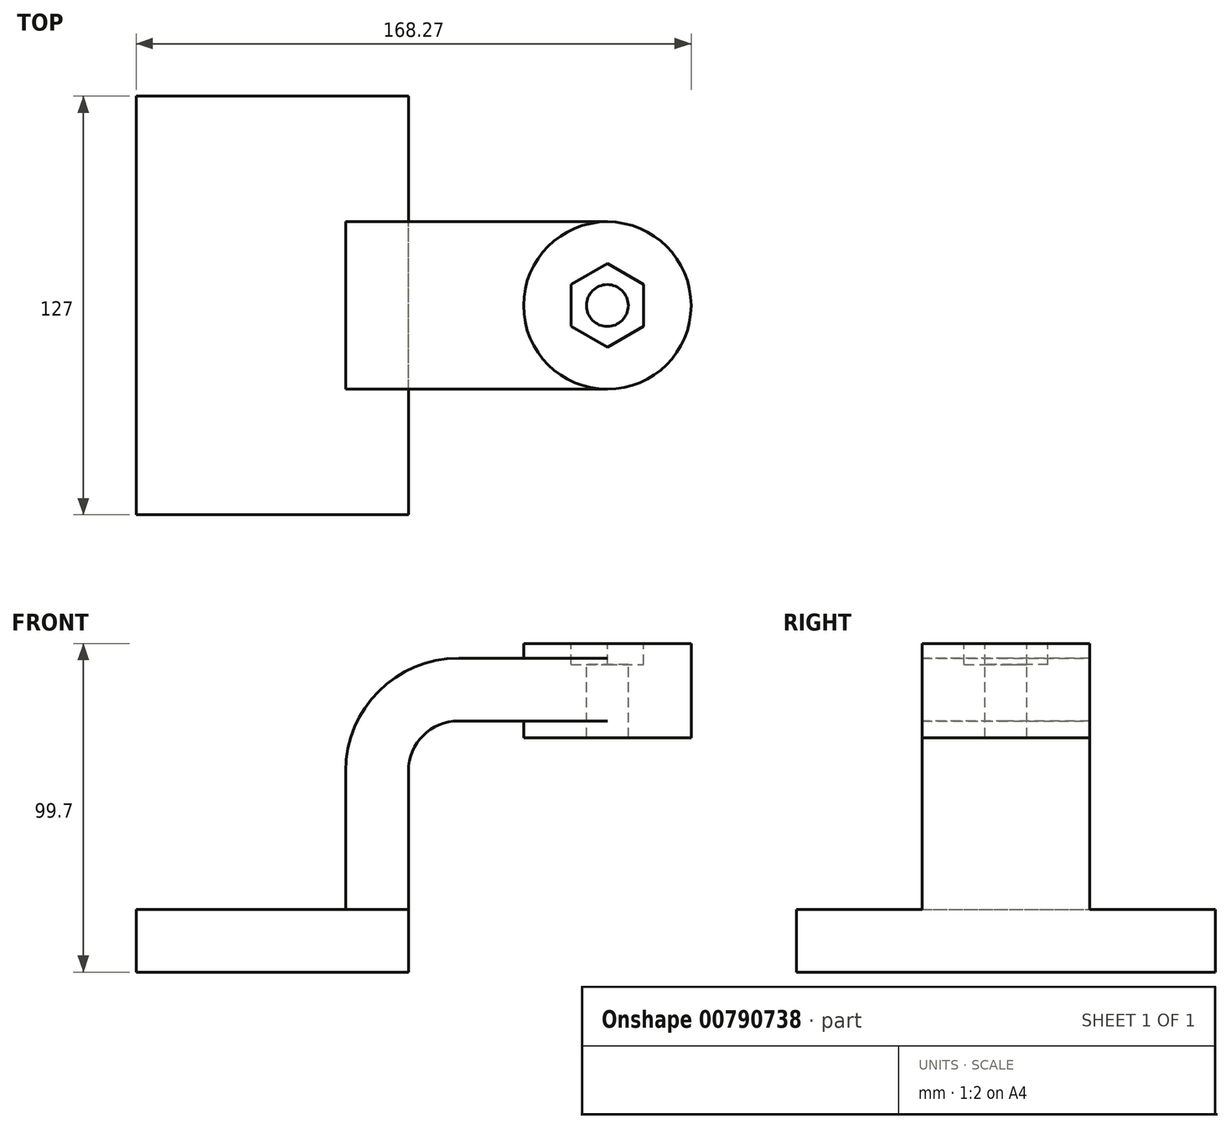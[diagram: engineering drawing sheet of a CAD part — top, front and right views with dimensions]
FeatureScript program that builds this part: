
annotation { "Feature Type Name" : "Feature", "Feature Type Description" : "" }
export const myFeature = defineFeature(function(context is Context, id is Id, definition is map)
    precondition{}
    {
        {
            var Q0;
            Q0=qCreatedBy(makeId("Front.planeOp"),FACE);
            var sketch = newSketch(context, id + "F0", { "sketchPlane" : qUnion([Q0])});
            skLineSegment(sketch, "E0.bottom", {"start": v(-41.28, 9.52) * mm, "end": v(41.28, 9.53) * mm});
            skLineSegment(sketch, "E0.top", {"start": v(-41.28, -9.52) * mm, "end": v(41.28, -9.52) * mm});
            skLineSegment(sketch, "E0.left", {"start": v(-41.28, 9.52) * mm, "end": v(-41.27, -9.53) * mm});
            skLineSegment(sketch, "E0.right", {"start": v(41.28, 9.53) * mm, "end": v(41.28, -9.52) * mm});
            skPoint(sketch, "E0.middle", {"position": v(0, 0) * mm});
            skLineSegment(sketch, "E1.bottom", {"start": v(76.2, 61.6) * mm, "end": v(127, 61.6) * mm});
            skLineSegment(sketch, "E1.top", {"start": v(76.2, 90.17) * mm, "end": v(127, 90.17) * mm});
            skLineSegment(sketch, "E1.left", {"start": v(76.2, 61.6) * mm, "end": v(76.2, 90.17) * mm});
            skLineSegment(sketch, "E1.right", {"start": v(127, 61.6) * mm, "end": v(127, 90.17) * mm});
            skPoint(sketch, "E1.middle", {"position": v(101.6, 75.88) * mm});
            skLineSegment(sketch, "E2", {"start": v(41.27, 9.53) * mm, "end": v(41.27, 51.44) * mm});
            skArc(sketch, "E3", {"start": v(41.27, 51.44) * mm, "mid": v(45.74, 62.21) * mm, "end": v(56.51, 66.68) * mm});
            skLineSegment(sketch, "E4", {"start": v(56.51, 66.68) * mm, "end": v(101.6, 66.68) * mm});
            skArc(sketch, "E5.1", {"start": v(22.22, 51.44) * mm, "mid": v(32.27, 75.68) * mm, "end": v(56.52, 85.73) * mm});
            skLineSegment(sketch, "E5.2", {"start": v(22.23, 9.53) * mm, "end": v(22.23, 51.44) * mm});
            skLineSegment(sketch, "E6.0", {"start": v(56.51, 85.73) * mm, "end": v(101.6, 85.73) * mm});
            skLineSegment(sketch, "E7", {"start": v(101.6, 61.6) * mm, "end": v(101.6, 90.17) * mm});
            skFitSpline(sketch, "E8", {"points": [v(-41.28, 9.53) * mm, v(56.52, 85.73) * mm], "startDerivative": vector(43.08, 48.74) * mm, "endDerivative": vector(237.38, -7.73) * mm});
            skSolve(sketch);
        }
        {
            var Q0;
            Q0=makeQuery(id+"F0.imprint","IMPRINT",FACE,{"disambiguationData":[TD([[makeQuery(id+"F0.imprint","IMPRINT",EDGE,{"derivedFrom":sQuery(id+"F0.wireOp",EDGE,"E0.top")}),1.0]])]});
            extrude(context, id + "F1", {"entities" : qUnion([Q0]), "endBound" : BoundingType.SYMMETRIC, "depth" : 127 * mm, "offsetDistance" : 25.4 * mm});
        }
        {
            var Q0;
            {var subQ1=sQuery(id+"F0.wireOp",EDGE,"E2");Q0=makeQuery(id+"F0.imprint","IMPRINT",FACE,{"disambiguationData":[TD([[makeQuery(id+"F0.imprint","IMPRINT",EDGE,{"derivedFrom":subQ1}),1.0]])]});}
            var Q1;
            {var subQ0=sQuery(id+"F0.wireOp",EDGE,"E4");var subQ1=sQuery(id+"F0.wireOp",EDGE,"E1.left");var subQ2=makeQuery(id+"F0.imprint","INTERSECT",VERTEX,{"derivedFrom":[subQ1,subQ0]});Q1=makeQuery(id+"F0.imprint","IMPRINT",FACE,{"disambiguationData":[TD([[makeQuery(id+"F0.imprint","IMPRINT",EDGE,{"disambiguationData":[TD([[subQ2,-1.0]])],"derivedFrom":subQ1}),-1.0]])]});}
            extrude(context, id + "F2", {"entities" : qUnion([Q0, Q1]), "operationType" : NewBodyOperationType.ADD, "endBound" : BoundingType.SYMMETRIC, "depth" : 50.8 * mm, "offsetDistance" : 25.4 * mm});
        }
        {
            var Q0;
            Q0=makeQuery(id+"F0.imprint","IMPRINT",FACE,{"disambiguationData":[TD([[makeQuery(id+"F0.imprint","IMPRINT",EDGE,{"derivedFrom":sQuery(id+"F0.wireOp",EDGE,"E5.1")}),1.0]])]});
            extrude(context, id + "F3", {"entities" : qUnion([Q0]), "operationType" : NewBodyOperationType.ADD, "endBound" : BoundingType.SYMMETRIC, "depth" : 12.7 * mm, "offsetDistance" : 25.4 * mm});
        }
        {
            var Q0;
            {var subQ0=sQuery(id+"F0.wireOp",EDGE,"E1.right");Q0=makeQuery(id+"F0.imprint","IMPRINT",FACE,{"disambiguationData":[TD([[makeQuery(id+"F0.imprint","IMPRINT",EDGE,{"derivedFrom":subQ0}),1.0]])]});}
            var Q1;
            Q1=sQuery(id+"F0.wireOp",EDGE,"E7");
            revolve(context, id + "F4", {"operationType" : NewBodyOperationType.ADD, "surfaceOperationType" : NewSurfaceOperationType.NEW, "entities" : qUnion([Q0]), "axis" : qUnion([Q1]), "revolveType" : RevolveType.FULL});
        }
        {
            var Q0;
            Q0=makeQuery(id+"F4.opRevolve","SWEPT_FACE",FACE,{"disambiguationData":[OSD([sQuery(id+"F0.wireOp",EDGE,"E1.top")])]});
            var sketch = newSketch(context, id + "F5", { "sketchPlane" : qUnion([Q0])});
            skCircle(sketch, "E9", {"center": v(101.6, 0) * mm, "radius": 6.35 * mm});
            skCircle(sketch, "E10.cCircle", {"center": v(101.6, 0) * mm, "radius": 12.7 * mm, "construction": true});
            skLineSegment(sketch, "E10.0", {"start": v(101.6, 12.7) * mm, "end": v(112.6, 6.35) * mm});
            skLineSegment(sketch, "E10.1", {"start": v(112.6, 6.35) * mm, "end": v(112.6, -6.35) * mm});
            skLineSegment(sketch, "E10.2", {"start": v(112.6, -6.35) * mm, "end": v(101.6, -12.7) * mm});
            skLineSegment(sketch, "E10.3", {"start": v(101.6, -12.7) * mm, "end": v(90.6, -6.35) * mm});
            skLineSegment(sketch, "E10.4", {"start": v(90.6, -6.35) * mm, "end": v(90.6, 6.35) * mm});
            skLineSegment(sketch, "E10.5", {"start": v(90.6, 6.35) * mm, "end": v(101.6, 12.7) * mm});
            skLineSegment(sketch, "E11", {"start": v(101.6, 0) * mm, "end": v(127, 0) * mm, "construction": true});
            skLineSegment(sketch, "E12", {"start": v(101.6, 0) * mm, "end": v(112.6, 6.35) * mm, "construction": true});
            skSolve(sketch);
        }
        {
            var Q0;
            Q0=makeQuery(id+"F5.imprint","IMPRINT",FACE,{"disambiguationData":[TD([[makeQuery(id+"F5.imprint","IMPRINT",EDGE,{"derivedFrom":sQuery(id+"F5.wireOp",EDGE,"E9")}),1.0]])]});
            extrude(context, id + "F6", {"entities" : qUnion([Q0]), "operationType" : NewBodyOperationType.REMOVE, "endBound" : BoundingType.THROUGH_ALL, "oppositeDirection" : true, "depth" : 25.4 * mm, "offsetDistance" : 25.4 * mm});
        }
        {
            var Q0;
            Q0 = qSketchRegion(id + "F5", true);
            extrude(context, id + "F7", {"entities" : qUnion([Q0]), "operationType" : NewBodyOperationType.REMOVE, "oppositeDirection" : true, "depth" : 6.35 * mm, "offsetDistance" : 25.4 * mm});
        }
    });
